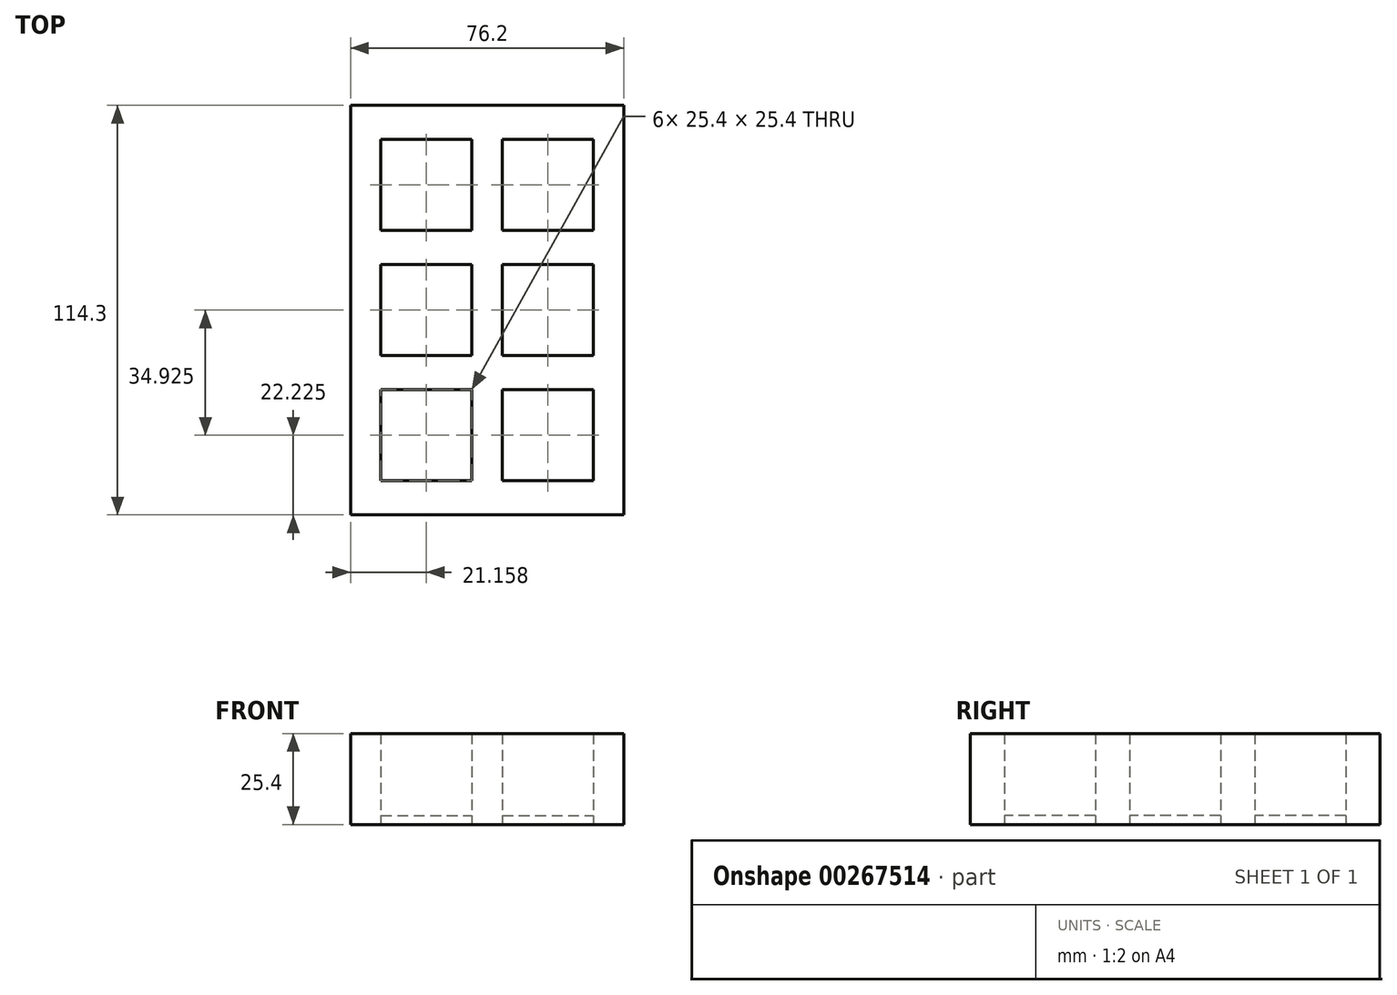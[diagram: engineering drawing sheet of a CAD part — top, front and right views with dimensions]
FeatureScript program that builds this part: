
annotation { "Feature Type Name" : "Feature", "Feature Type Description" : "" }
export const myFeature = defineFeature(function(context is Context, id is Id, definition is map)
    precondition{}
    {
        {
            var Q0;
            Q0=qCreatedBy(makeId("Top.planeOp"),FACE);
            var sketch = newSketch(context, id + "F0", { "sketchPlane" : qUnion([Q0])});
            skLineSegment(sketch, "E0.bottom", {"start": v(38.1, 57.15) * mm, "end": v(-38.1, 57.15) * mm});
            skLineSegment(sketch, "E0.top", {"start": v(38.1, -57.15) * mm, "end": v(-38.1, -57.15) * mm});
            skLineSegment(sketch, "E0.left", {"start": v(38.1, 57.15) * mm, "end": v(38.1, -57.15) * mm});
            skLineSegment(sketch, "E0.right", {"start": v(-38.1, 57.15) * mm, "end": v(-38.1, -57.15) * mm});
            skPoint(sketch, "E0.middle", {"position": v(0, 0) * mm});
            skLineSegment(sketch, "E1.bottom", {"start": v(-29.64, 47.62) * mm, "end": v(-4.24, 47.62) * mm});
            skLineSegment(sketch, "E1.top", {"start": v(-29.64, 22.22) * mm, "end": v(-4.24, 22.22) * mm});
            skLineSegment(sketch, "E1.left", {"start": v(-29.64, 47.62) * mm, "end": v(-29.64, 22.22) * mm});
            skLineSegment(sketch, "E1.right", {"start": v(-4.24, 47.62) * mm, "end": v(-4.24, 22.22) * mm});
            skLineSegment(sketch, "E2.bottom", {"start": v(4.22, 47.62) * mm, "end": v(29.62, 47.62) * mm});
            skLineSegment(sketch, "E2.top", {"start": v(4.22, 22.23) * mm, "end": v(29.62, 22.23) * mm});
            skLineSegment(sketch, "E2.left", {"start": v(4.22, 47.62) * mm, "end": v(4.22, 22.23) * mm});
            skLineSegment(sketch, "E2.right", {"start": v(29.62, 47.63) * mm, "end": v(29.62, 22.23) * mm});
            skLineSegment(sketch, "E3.bottom", {"start": v(-29.64, 12.7) * mm, "end": v(-4.24, 12.7) * mm});
            skLineSegment(sketch, "E3.top", {"start": v(-29.64, -12.7) * mm, "end": v(-4.24, -12.7) * mm});
            skLineSegment(sketch, "E3.left", {"start": v(-29.64, 12.7) * mm, "end": v(-29.64, -12.7) * mm});
            skLineSegment(sketch, "E3.right", {"start": v(-4.24, 12.7) * mm, "end": v(-4.24, -12.7) * mm});
            skLineSegment(sketch, "E4.bottom", {"start": v(-29.64, -22.23) * mm, "end": v(-4.24, -22.23) * mm});
            skLineSegment(sketch, "E4.top", {"start": v(-29.64, -47.63) * mm, "end": v(-4.24, -47.63) * mm});
            skLineSegment(sketch, "E4.left", {"start": v(-29.64, -22.23) * mm, "end": v(-29.64, -47.63) * mm});
            skLineSegment(sketch, "E4.right", {"start": v(-4.24, -22.23) * mm, "end": v(-4.24, -47.63) * mm});
            skLineSegment(sketch, "E5.bottom", {"start": v(4.22, 12.7) * mm, "end": v(29.62, 12.7) * mm});
            skLineSegment(sketch, "E5.top", {"start": v(4.22, -12.7) * mm, "end": v(29.62, -12.7) * mm});
            skLineSegment(sketch, "E5.left", {"start": v(4.22, 12.7) * mm, "end": v(4.22, -12.7) * mm});
            skLineSegment(sketch, "E5.right", {"start": v(29.62, 12.7) * mm, "end": v(29.62, -12.7) * mm});
            skLineSegment(sketch, "E6.bottom", {"start": v(4.22, -22.23) * mm, "end": v(29.62, -22.23) * mm});
            skLineSegment(sketch, "E6.top", {"start": v(4.22, -47.62) * mm, "end": v(29.62, -47.62) * mm});
            skLineSegment(sketch, "E6.left", {"start": v(4.22, -22.23) * mm, "end": v(4.22, -47.62) * mm});
            skLineSegment(sketch, "E6.right", {"start": v(29.62, -22.23) * mm, "end": v(29.62, -47.62) * mm});
            skSolve(sketch);
        }
        {
            var Q0;
            Q0=makeQuery(id+"F0.imprint","IMPRINT",FACE,{"disambiguationData":[TD([[makeQuery(id+"F0.imprint","IMPRINT",EDGE,{"derivedFrom":sQuery(id+"F0.wireOp",EDGE,"E0.bottom")}),1.0]])]});
            extrude(context, id + "F1", {"entities" : qUnion([Q0]), "depth" : 25.4 * mm});
        }
        {
            var Q0;
            Q0=makeQuery(id+"F0.imprint","IMPRINT",FACE,{"disambiguationData":[TD([[makeQuery(id+"F0.imprint","IMPRINT",EDGE,{"derivedFrom":sQuery(id+"F0.wireOp",EDGE,"E1.bottom")}),-1.0]])]});
            var Q1;
            Q1=makeQuery(id+"F0.imprint","IMPRINT",FACE,{"disambiguationData":[TD([[makeQuery(id+"F0.imprint","IMPRINT",EDGE,{"derivedFrom":sQuery(id+"F0.wireOp",EDGE,"E2.bottom")}),-1.0]])]});
            var Q2;
            Q2=makeQuery(id+"F0.imprint","IMPRINT",FACE,{"disambiguationData":[TD([[makeQuery(id+"F0.imprint","IMPRINT",EDGE,{"derivedFrom":sQuery(id+"F0.wireOp",EDGE,"E3.bottom")}),-1.0]])]});
            var Q3;
            Q3=makeQuery(id+"F0.imprint","IMPRINT",FACE,{"disambiguationData":[TD([[makeQuery(id+"F0.imprint","IMPRINT",EDGE,{"derivedFrom":sQuery(id+"F0.wireOp",EDGE,"E5.bottom")}),-1.0]])]});
            var Q4;
            Q4=makeQuery(id+"F0.imprint","IMPRINT",FACE,{"disambiguationData":[TD([[makeQuery(id+"F0.imprint","IMPRINT",EDGE,{"derivedFrom":sQuery(id+"F0.wireOp",EDGE,"E4.bottom")}),-1.0]])]});
            var Q5;
            Q5=makeQuery(id+"F0.imprint","IMPRINT",FACE,{"disambiguationData":[TD([[makeQuery(id+"F0.imprint","IMPRINT",EDGE,{"derivedFrom":sQuery(id+"F0.wireOp",EDGE,"E6.bottom")}),-1.0]])]});
            extrude(context, id + "F2", {"entities" : qUnion([Q0, Q1, Q2, Q3, Q4, Q5]), "depth" : 2.54 * mm});
        }
    });
